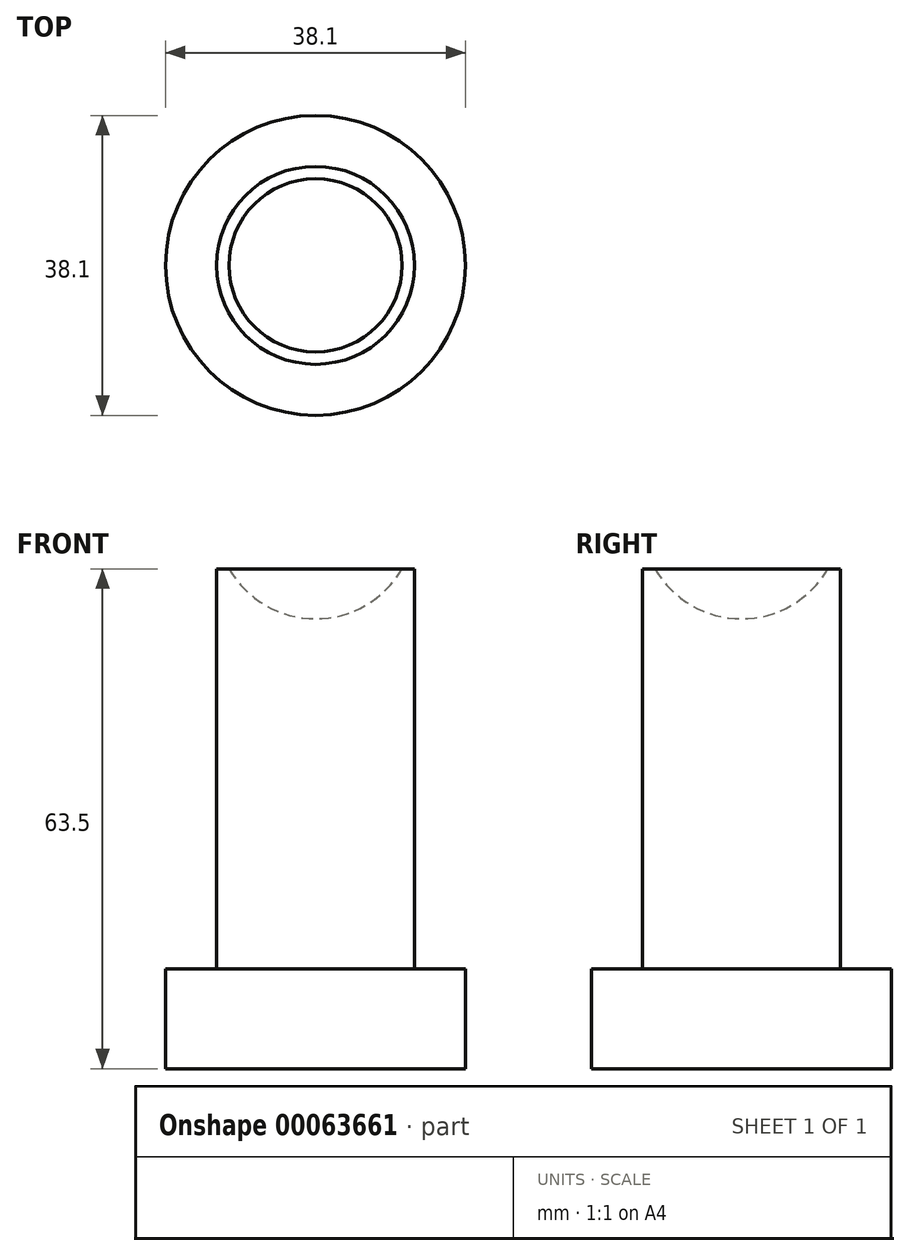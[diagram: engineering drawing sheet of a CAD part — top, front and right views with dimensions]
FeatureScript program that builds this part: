
annotation { "Feature Type Name" : "Feature", "Feature Type Description" : "" }
export const myFeature = defineFeature(function(context is Context, id is Id, definition is map)
    precondition{}
    {
        {
            var Q0;
            Q0=qCreatedBy(makeId("Top.planeOp"),FACE);
            var sketch = newSketch(context, id + "F0", { "sketchPlane" : qUnion([Q0])});
            skCircle(sketch, "E0", {"center": v(0, 0) * mm, "radius": 19.05 * mm});
            skSolve(sketch);
        }
        {
            var Q0;
            Q0=makeQuery(id+"F0.imprint","IMPRINT",FACE,{"disambiguationData":[TD([[makeQuery(id+"F0.imprint","IMPRINT",EDGE,{"derivedFrom":sQuery(id+"F0.wireOp",EDGE,"E0")}),1.0]])]});
            extrude(context, id + "F1", {"entities" : qUnion([Q0]), "depth" : 12.7 * mm});
        }
        {
            var Q0;
            Q0=makeQuery(id+"F1.opExtrude","CAP_FACE",FACE,{"disambiguationData":[OSD([sQuery(id+"F0.wireOp",EDGE,"E0")])],"isStart":false});
            var sketch = newSketch(context, id + "F2", { "sketchPlane" : qUnion([Q0])});
            skCircle(sketch, "E1", {"center": v(0, 0) * mm, "radius": 12.57 * mm});
            skSolve(sketch);
        }
        {
            var Q0;
            Q0=makeQuery(id+"F2.imprint","IMPRINT",FACE,{"disambiguationData":[TD([[makeQuery(id+"F2.imprint","IMPRINT",EDGE,{"derivedFrom":sQuery(id+"F2.wireOp",EDGE,"E1")}),1.0]])]});
            extrude(context, id + "F3", {"entities" : qUnion([Q0]), "operationType" : NewBodyOperationType.ADD, "depth" : 50.8 * mm});
        }
        {
            var Q0;
            Q0=qCreatedBy(makeId("Right.planeOp"),FACE);
            var sketch = newSketch(context, id + "F4", { "sketchPlane" : qUnion([Q0])});
            skArc(sketch, "E2", {"start": v(-12.7, 69.85) * mm, "mid": v(0, 57.15) * mm, "end": v(12.7, 69.85) * mm});
            skLineSegment(sketch, "E3", {"start": v(12.7, 69.85) * mm, "end": v(-12.7, 69.85) * mm});
            skSolve(sketch);
        }
        {
            var Q0;
            Q0=makeQuery(id+"F4.imprint","IMPRINT",FACE,{"disambiguationData":[TD([[makeQuery(id+"F4.imprint","IMPRINT",EDGE,{"derivedFrom":sQuery(id+"F4.wireOp",EDGE,"E2")}),1.0]])]});
            var Q1;
            Q1=sQuery(id+"F4.wireOp",EDGE,"E3");
            revolve(context, id + "F5", {"operationType" : NewBodyOperationType.REMOVE, "entities" : qUnion([Q0]), "axis" : qUnion([Q1]), "revolveType" : RevolveType.FULL, "oppositeDirection" : true});
        }
    });
